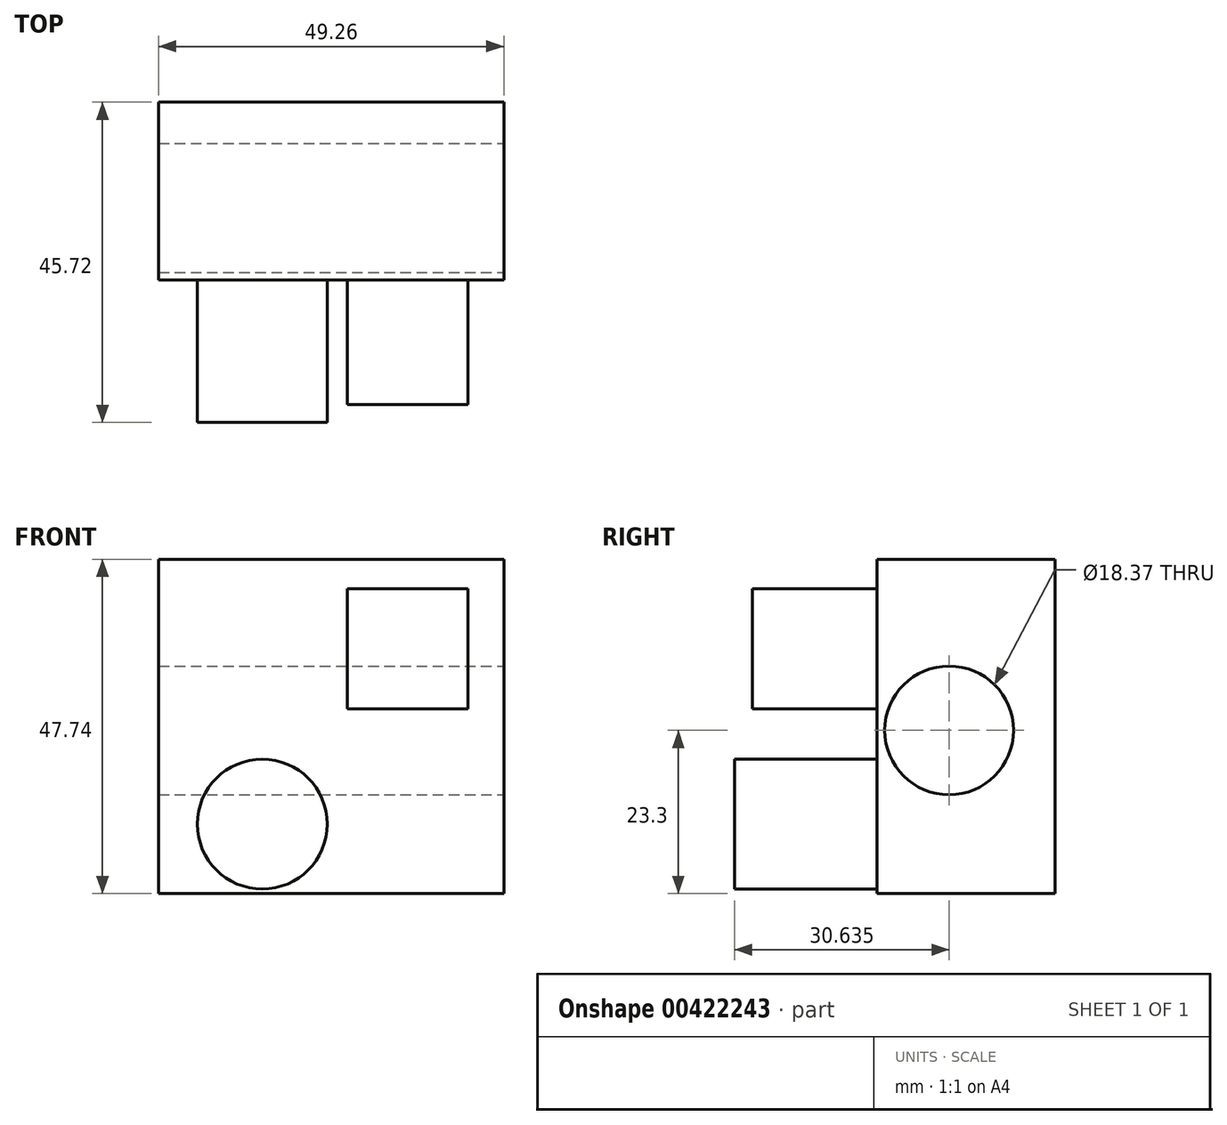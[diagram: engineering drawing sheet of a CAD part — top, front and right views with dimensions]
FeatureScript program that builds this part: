
annotation { "Feature Type Name" : "Feature", "Feature Type Description" : "" }
export const myFeature = defineFeature(function(context is Context, id is Id, definition is map)
    precondition{}
    {
        {
            var Q0;
            Q0=qCreatedBy(makeId("Front.planeOp"),FACE);
            var sketch = newSketch(context, id + "F0", { "sketchPlane" : qUnion([Q0])});
            skLineSegment(sketch, "E0.bottom", {"start": v(-20.62, 24.44) * mm, "end": v(28.64, 24.44) * mm});
            skLineSegment(sketch, "E0.top", {"start": v(-20.62, -23.3) * mm, "end": v(28.64, -23.3) * mm});
            skLineSegment(sketch, "E0.left", {"start": v(-20.62, 24.44) * mm, "end": v(-20.62, -23.3) * mm});
            skLineSegment(sketch, "E0.right", {"start": v(28.64, 24.44) * mm, "end": v(28.64, -23.3) * mm});
            skSolve(sketch);
        }
        {
            var Q0;
            Q0 = qSketchRegion(id + "F0", true);
            extrude(context, id + "F1", {"entities" : qUnion([Q0]), "depth" : 25.4 * mm});
        }
        {
            var Q0;
            Q0=makeQuery(id+"F1.opExtrude","CAP_FACE",FACE,{"disambiguationData":[OSD([sQuery(id+"F0.wireOp",EDGE,"E0.bottom"),sQuery(id+"F0.wireOp",EDGE,"E0.top"),sQuery(id+"F0.wireOp",EDGE,"E0.left"),sQuery(id+"F0.wireOp",EDGE,"E0.right")])],"isStart":false});
            var sketch = newSketch(context, id + "F2", { "sketchPlane" : qUnion([Q0])});
            skLineSegment(sketch, "E1.bottom", {"start": v(6.3, 20.24) * mm, "end": v(23.49, 20.24) * mm});
            skLineSegment(sketch, "E1.top", {"start": v(6.3, 3.06) * mm, "end": v(23.49, 3.06) * mm});
            skLineSegment(sketch, "E1.left", {"start": v(6.3, 20.24) * mm, "end": v(6.3, 3.06) * mm});
            skLineSegment(sketch, "E1.right", {"start": v(23.49, 20.24) * mm, "end": v(23.49, 3.06) * mm});
            skSolve(sketch);
        }
        {
            var Q0;
            Q0 = qSketchRegion(id + "F2", true);
            extrude(context, id + "F3", {"entities" : qUnion([Q0]), "operationType" : NewBodyOperationType.ADD, "depth" : 17.78 * mm});
        }
        {
            var Q0;
            Q0=makeQuery(id+"F1.opExtrude","CAP_FACE",FACE,{"disambiguationData":[OSD([sQuery(id+"F0.wireOp",EDGE,"E0.bottom"),sQuery(id+"F0.wireOp",EDGE,"E0.top"),sQuery(id+"F0.wireOp",EDGE,"E0.left"),sQuery(id+"F0.wireOp",EDGE,"E0.right")])],"isStart":false});
            var sketch = newSketch(context, id + "F4", { "sketchPlane" : qUnion([Q0])});
            skCircle(sketch, "E2", {"center": v(-5.83, -13.38) * mm, "radius": 9.27 * mm});
            skSolve(sketch);
        }
        {
            var Q0;
            Q0 = qSketchRegion(id + "F4", true);
            extrude(context, id + "F5", {"entities" : qUnion([Q0]), "operationType" : NewBodyOperationType.ADD, "depth" : 20.32 * mm});
        }
        {
            var Q0;
            Q0=makeQuery(id+"F1.opExtrude","SWEPT_FACE",FACE,{"disambiguationData":[OSD([sQuery(id+"F0.wireOp",EDGE,"E0.right")])]});
            var sketch = newSketch(context, id + "F6", { "sketchPlane" : qUnion([Q0])});
            skCircle(sketch, "E3", {"center": v(-15.09, 0) * mm, "radius": 9.18 * mm});
            skSolve(sketch);
        }
        {
            var Q0;
            Q0 = qSketchRegion(id + "F6", true);
            extrude(context, id + "F7", {"entities" : qUnion([Q0]), "operationType" : NewBodyOperationType.REMOVE, "oppositeDirection" : true, "depth" : 50.8 * mm});
        }
    });
